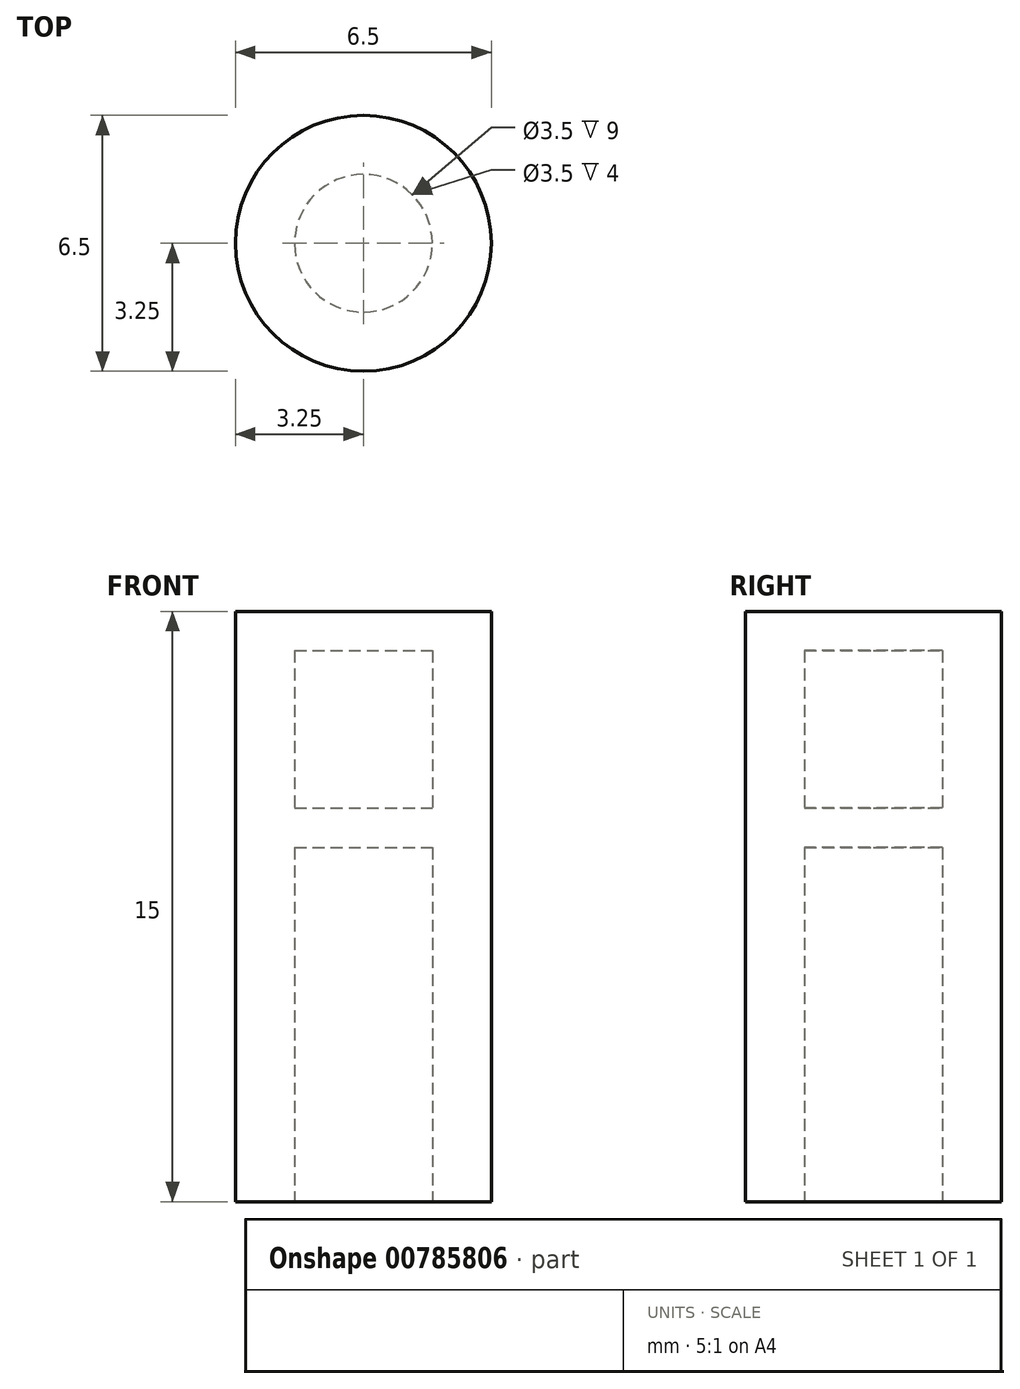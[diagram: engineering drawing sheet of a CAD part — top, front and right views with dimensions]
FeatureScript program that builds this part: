
annotation { "Feature Type Name" : "Feature", "Feature Type Description" : "" }
export const myFeature = defineFeature(function(context is Context, id is Id, definition is map)
    precondition{}
    {
        {
            var Q0;
            Q0=qCreatedBy(makeId("Top.planeOp"),FACE);
            var sketch = newSketch(context, id + "F0", { "sketchPlane" : qUnion([Q0])});
            skCircle(sketch, "E0", {"center": v(0, 0) * mm, "radius": 3.25 * mm});
            skSolve(sketch);
        }
        {
            var Q0;
            Q0=makeQuery(id+"F0.imprint","IMPRINT",FACE,{"disambiguationData":[TD([[makeQuery(id+"F0.imprint","IMPRINT",EDGE,{"derivedFrom":sQuery(id+"F0.wireOp",EDGE,"E0")}),1.0]])]});
            extrude(context, id + "F1", {"entities" : qUnion([Q0]), "depth" : 15 * mm, "offsetDistance" : 25 * mm});
        }
        {
            var Q0;
            Q0=makeQuery(id+"F1.opExtrude","CAP_FACE",FACE,{"disambiguationData":[OSD([sQuery(id+"F0.wireOp",EDGE,"E0")])],"isStart":true});
            var sketch = newSketch(context, id + "F2", { "sketchPlane" : qUnion([Q0])});
            skCircle(sketch, "E1", {"center": v(0, 0) * mm, "radius": 1.75 * mm});
            skSolve(sketch);
        }
        {
            var Q0;
            Q0=makeQuery(id+"F2.imprint","IMPRINT",FACE,{"disambiguationData":[TD([[makeQuery(id+"F2.imprint","IMPRINT",EDGE,{"derivedFrom":sQuery(id+"F2.wireOp",EDGE,"E1")}),1.0]])]});
            extrude(context, id + "F3", {"entities" : qUnion([Q0]), "operationType" : NewBodyOperationType.REMOVE, "oppositeDirection" : true, "depth" : 9 * mm, "offsetDistance" : 25 * mm});
        }
        {
            var Q0;
            Q0=makeQuery(id+"F3.boolean.opBoolean","COPY",FACE,{"derivedFrom":makeQuery(id+"F3.opExtrude","CAP_FACE",FACE,{"disambiguationData":[OSD([sQuery(id+"F2.wireOp",EDGE,"E1")])],"isStart":false})});
            cPlane(context, id + "F4", {"entities" : qUnion([Q0]), "cplaneType" : CPlaneType.OFFSET, "offset" : 1 * mm, "oppositeDirection" : true, "width" : 150 * mm, "height" : 150 * mm});
        }
        {
            var Q0;
            Q0=qCreatedBy(id+"F4.planeOp",FACE);
            var sketch = newSketch(context, id + "F5", { "sketchPlane" : qUnion([Q0])});
            skCircle(sketch, "E2.0", {"center": v(0, 0) * mm, "radius": 1.75 * mm});
            skSolve(sketch);
        }
        {
            var Q0;
            Q0 = qSketchRegion(id + "F5", true);
            extrude(context, id + "F6", {"entities" : qUnion([Q0]), "operationType" : NewBodyOperationType.REMOVE, "oppositeDirection" : true, "depth" : 4 * mm, "offsetDistance" : 25 * mm});
        }
    });
